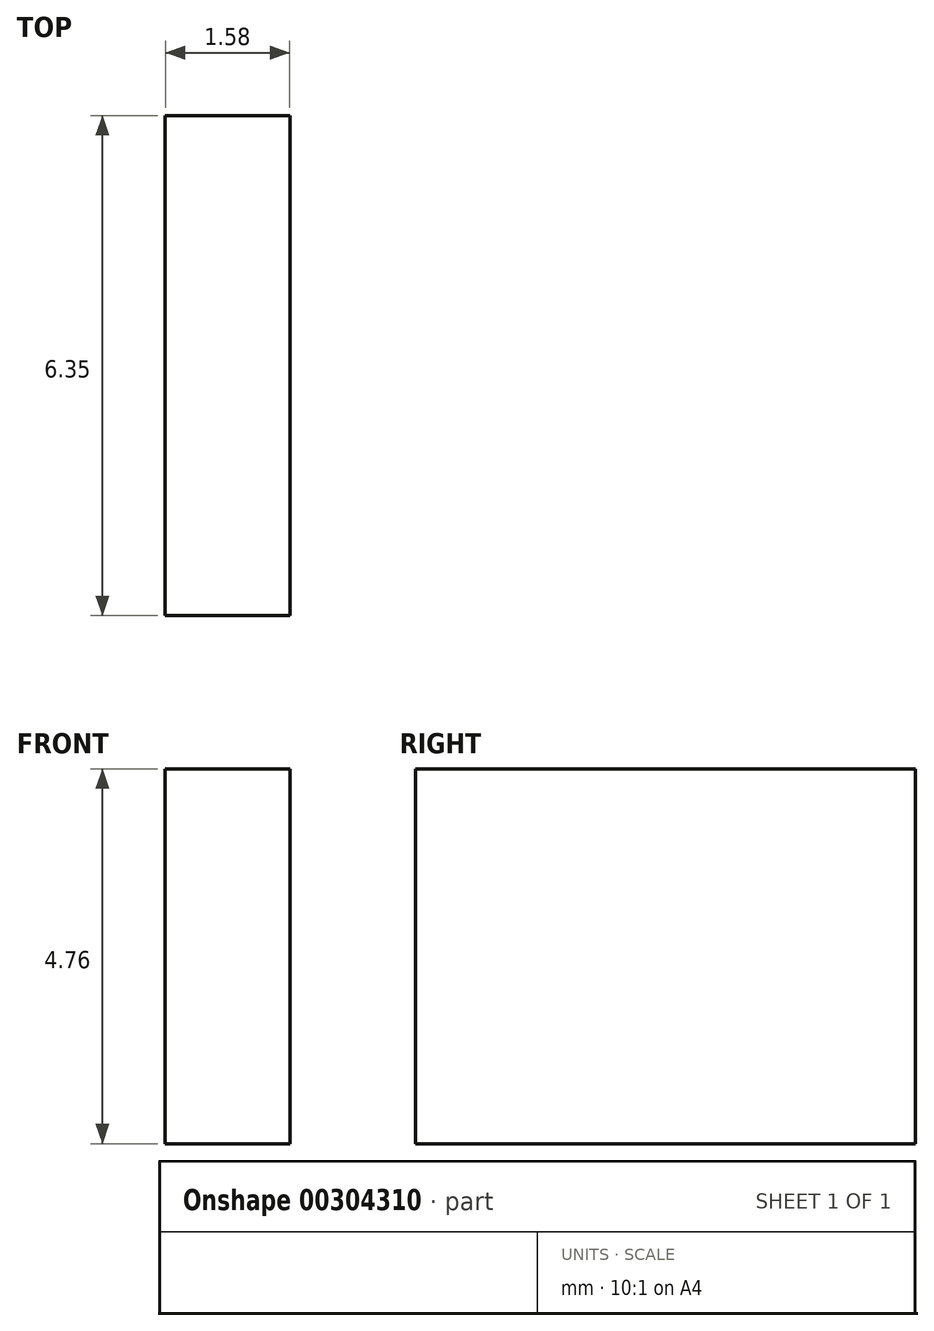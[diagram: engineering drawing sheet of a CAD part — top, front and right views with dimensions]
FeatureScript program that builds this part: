
annotation { "Feature Type Name" : "Feature", "Feature Type Description" : "" }
export const myFeature = defineFeature(function(context is Context, id is Id, definition is map)
    precondition{}
    {
        {
            var Q0;
            Q0=qCreatedBy(makeId("Front.planeOp"),FACE);
            var sketch = newSketch(context, id + "F0", { "sketchPlane" : qUnion([Q0])});
            skLineSegment(sketch, "E0.bottom", {"start": v(-0.8, 0) * mm, "end": v(0.8, 0) * mm});
            skLineSegment(sketch, "E0.top", {"start": v(-0.8, 4.76) * mm, "end": v(0.8, 4.76) * mm});
            skLineSegment(sketch, "E0.left", {"start": v(-0.8, 0) * mm, "end": v(-0.8, 4.76) * mm});
            skLineSegment(sketch, "E0.right", {"start": v(0.8, 0) * mm, "end": v(0.8, 4.76) * mm});
            skSolve(sketch);
        }
        {
            var Q0;
            Q0 = qSketchRegion(id + "F0", true);
            extrude(context, id + "F1", {"entities" : qUnion([Q0]), "depth" : 6.35 * mm});
        }
    });
